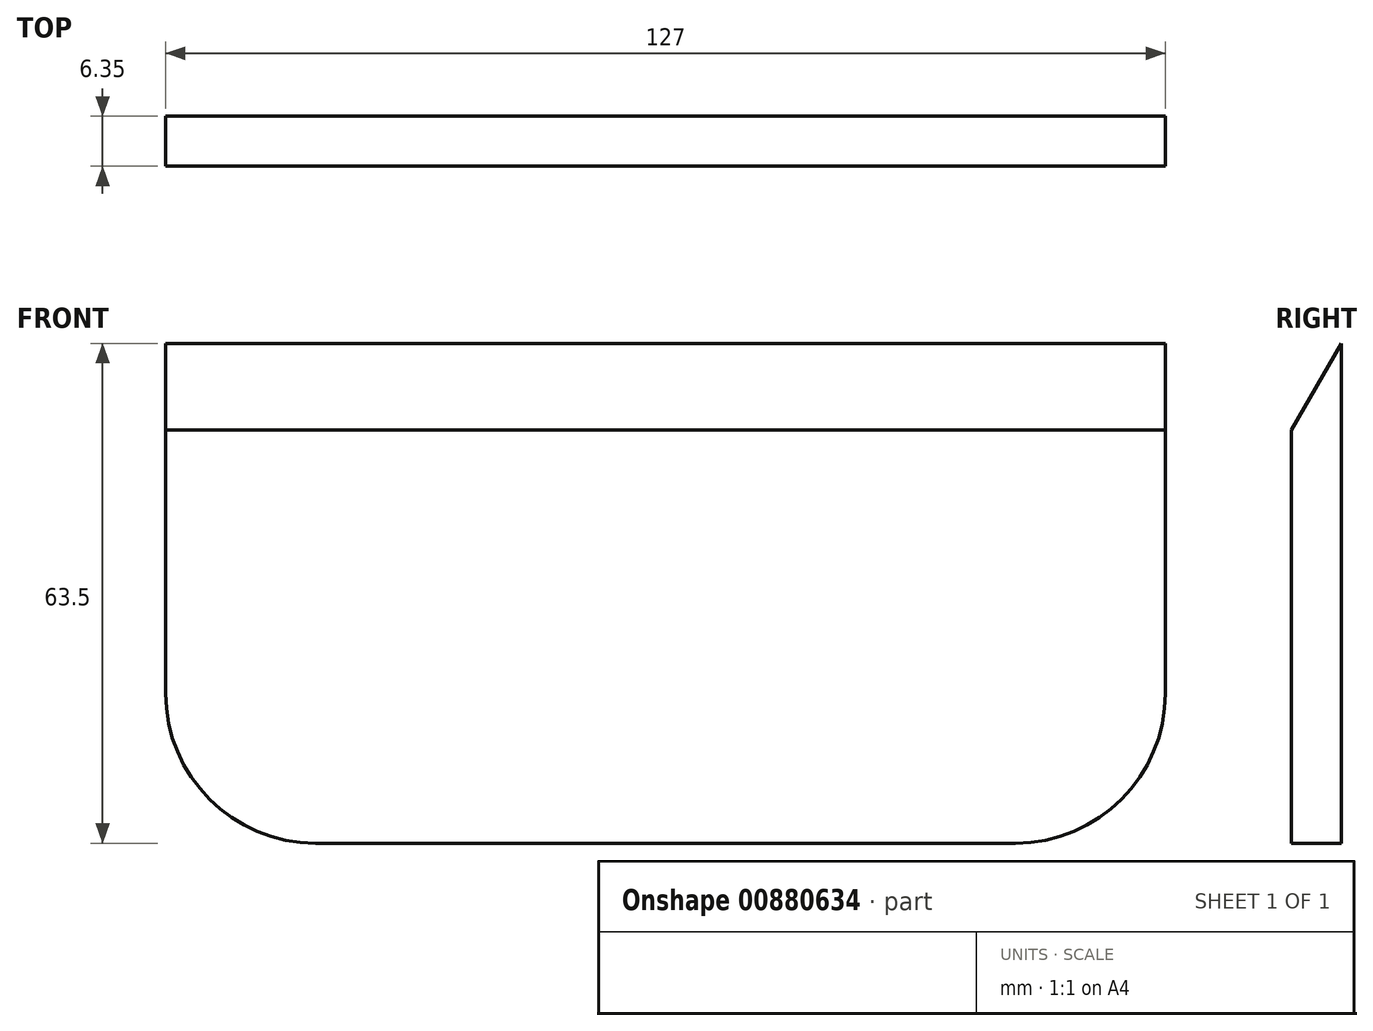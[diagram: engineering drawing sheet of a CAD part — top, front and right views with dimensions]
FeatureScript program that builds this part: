
annotation { "Feature Type Name" : "Feature", "Feature Type Description" : "" }
export const myFeature = defineFeature(function(context is Context, id is Id, definition is map)
    precondition{}
    {
        {
            var Q0;
            Q0=qCreatedBy(makeId("Right.planeOp"),FACE);
            var sketch = newSketch(context, id + "F0", { "sketchPlane" : qUnion([Q0])});
            skLineSegment(sketch, "E0", {"start": v(0, 0) * mm, "end": v(0, -63.5) * mm});
            skLineSegment(sketch, "E1", {"start": v(0, -63.5) * mm, "end": v(-6.35, -63.5) * mm});
            skLineSegment(sketch, "E2", {"start": v(-6.35, -63.5) * mm, "end": v(-6.35, -11) * mm});
            skLineSegment(sketch, "E3", {"start": v(-6.35, -11) * mm, "end": v(0, 0) * mm});
            skSolve(sketch);
        }
        {
            var Q0;
            Q0=qSketchRegion(id+"F0",true);
            extrude(context, id + "F1", {"entities" : qUnion([Q0]), "depth" : 127 * mm});
        }
        {
            var Q0;
            Q0=qCreatedBy(makeId("Front.planeOp"),FACE);
            var sketch = newSketch(context, id + "F2", { "sketchPlane" : qUnion([Q0])});
            skLineSegment(sketch, "E4", {"start": v(127, -30.05) * mm, "end": v(127, -44.45) * mm});
            skLineSegment(sketch, "E5", {"start": v(107.95, -63.5) * mm, "end": v(99.7, -63.5) * mm});
            skLineSegment(sketch, "E6", {"start": v(99.7, -63.5) * mm, "end": v(99.7, -83.43) * mm});
            skLineSegment(sketch, "E7", {"start": v(99.7, -83.43) * mm, "end": v(143.54, -83.43) * mm});
            skLineSegment(sketch, "E8", {"start": v(143.54, -83.43) * mm, "end": v(143.54, -31.04) * mm});
            skLineSegment(sketch, "E9", {"start": v(143.54, -31.04) * mm, "end": v(127, -30.05) * mm});
            skPoint(sketch, "E10.visualSharp", {"position": v(127, -63.5) * mm});
            skArc(sketch, "E10.filletArc", {"start": v(107.95, -63.5) * mm, "mid": v(121.42, -57.92) * mm, "end": v(127, -44.45) * mm});
            skLineSegment(sketch, "E11", {"start": v(0, -33.84) * mm, "end": v(0, -44.45) * mm});
            skLineSegment(sketch, "E12", {"start": v(19.05, -63.5) * mm, "end": v(44.85, -63.5) * mm});
            skLineSegment(sketch, "E13", {"start": v(44.85, -63.5) * mm, "end": v(46.44, -77.65) * mm});
            skLineSegment(sketch, "E14", {"start": v(46.44, -77.65) * mm, "end": v(-28.9, -77.65) * mm});
            skLineSegment(sketch, "E15", {"start": v(-28.9, -77.65) * mm, "end": v(-28.9, -33.25) * mm});
            skLineSegment(sketch, "E16", {"start": v(-28.9, -33.25) * mm, "end": v(0, -33.84) * mm});
            skPoint(sketch, "E17.visualSharp", {"position": v(0, -63.5) * mm});
            skArc(sketch, "E17.filletArc", {"start": v(0, -44.45) * mm, "mid": v(5.58, -57.92) * mm, "end": v(19.05, -63.5) * mm});
            skSolve(sketch);
        }
        {
            var Q0;
            Q0=makeQuery(id+"F2.imprint","IMPRINT",FACE,{"disambiguationData":[TD([[makeQuery(id+"F2.imprint","IMPRINT",EDGE,{"derivedFrom":sQuery(id+"F2.wireOp",EDGE,"E11")}),-1.0]])]});
            var Q1;
            Q1=makeQuery(id+"F2.imprint","IMPRINT",FACE,{"disambiguationData":[TD([[makeQuery(id+"F2.imprint","IMPRINT",EDGE,{"derivedFrom":sQuery(id+"F2.wireOp",EDGE,"E4")}),1.0]])]});
            extrude(context, id + "F3", {"entities" : qUnion([Q0, Q1]), "operationType" : NewBodyOperationType.REMOVE, "depth" : 7.37 * mm, "offsetDistance" : 25.4 * mm});
        }
    });
